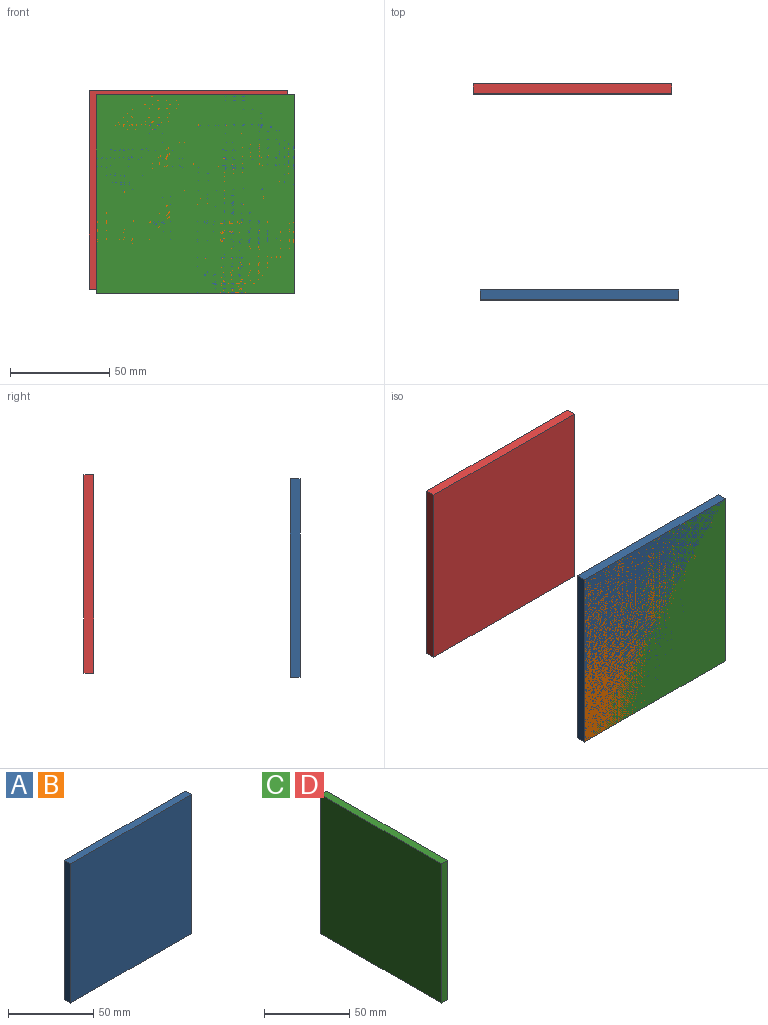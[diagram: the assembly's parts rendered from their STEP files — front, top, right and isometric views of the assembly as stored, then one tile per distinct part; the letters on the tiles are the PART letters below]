
ASSEMBLY  parts=4 mates=2
PART A: 6 faces, bbox 100x5x100 mm
  f0: plane 100x5mm, normal (-1,0,0), area 500mm2, adj f1,f3,f4,f5
  f1: plane 100x5mm, normal (0,0,-1), area 500mm2, adj f0,f2,f4,f5
  f2: plane 100x5mm, normal (1,0,0), area 500mm2, adj f1,f3,f4,f5
  f3: plane 100x5mm, normal (0,0,1), area 500mm2, adj f0,f2,f4,f5
  f4: plane 100x100mm, normal (0,-1,0), area 10000mm2, adj f0,f1,f2,f3
  f5: plane 100x100mm, normal (0,1,0), area 10000mm2, adj f0,f1,f2,f3
PART B: same geometry as A
PART C: 6 faces, bbox 5x100x100 mm
  f0: plane 100x5mm, normal (0,-1,0), area 500mm2, adj f1,f3,f4,f5
  f1: plane 100x5mm, normal (0,0,-1), area 500mm2, adj f0,f2,f4,f5
  f2: plane 100x5mm, normal (0,1,0), area 500mm2, adj f1,f3,f4,f5
  f3: plane 100x5mm, normal (0,0,1), area 500mm2, adj f0,f2,f4,f5
  f4: plane 100x100mm, normal (1,0,0), area 10000mm2, adj f0,f1,f2,f3
  f5: plane 100x100mm, normal (-1,0,0), area 10000mm2, adj f0,f1,f2,f3
PART D: same geometry as C
PLACE A rot(axis=(0,-1,0),90deg) t=(-55.94,-63.6,-4.19)mm
PLACE B t=(-54.86,-63.6,-4.78)mm
PLACE C rot(axis=(0.71,-0.71,0),180deg) t=(-147.08,-63.6,15.16)mm
PLACE D rot(axis=(0,0,-1),90deg) t=(32.1,40.23,-23.06)mm
MATE fastened A.f4 <-> C.f4  axis (0,-1,0) through (-55.69,-68.6,-5.02)mm
MATE slider A.f4 <-> B.f4  axis (0,-1,0) through (-55.69,-68.6,-5.02)mm
